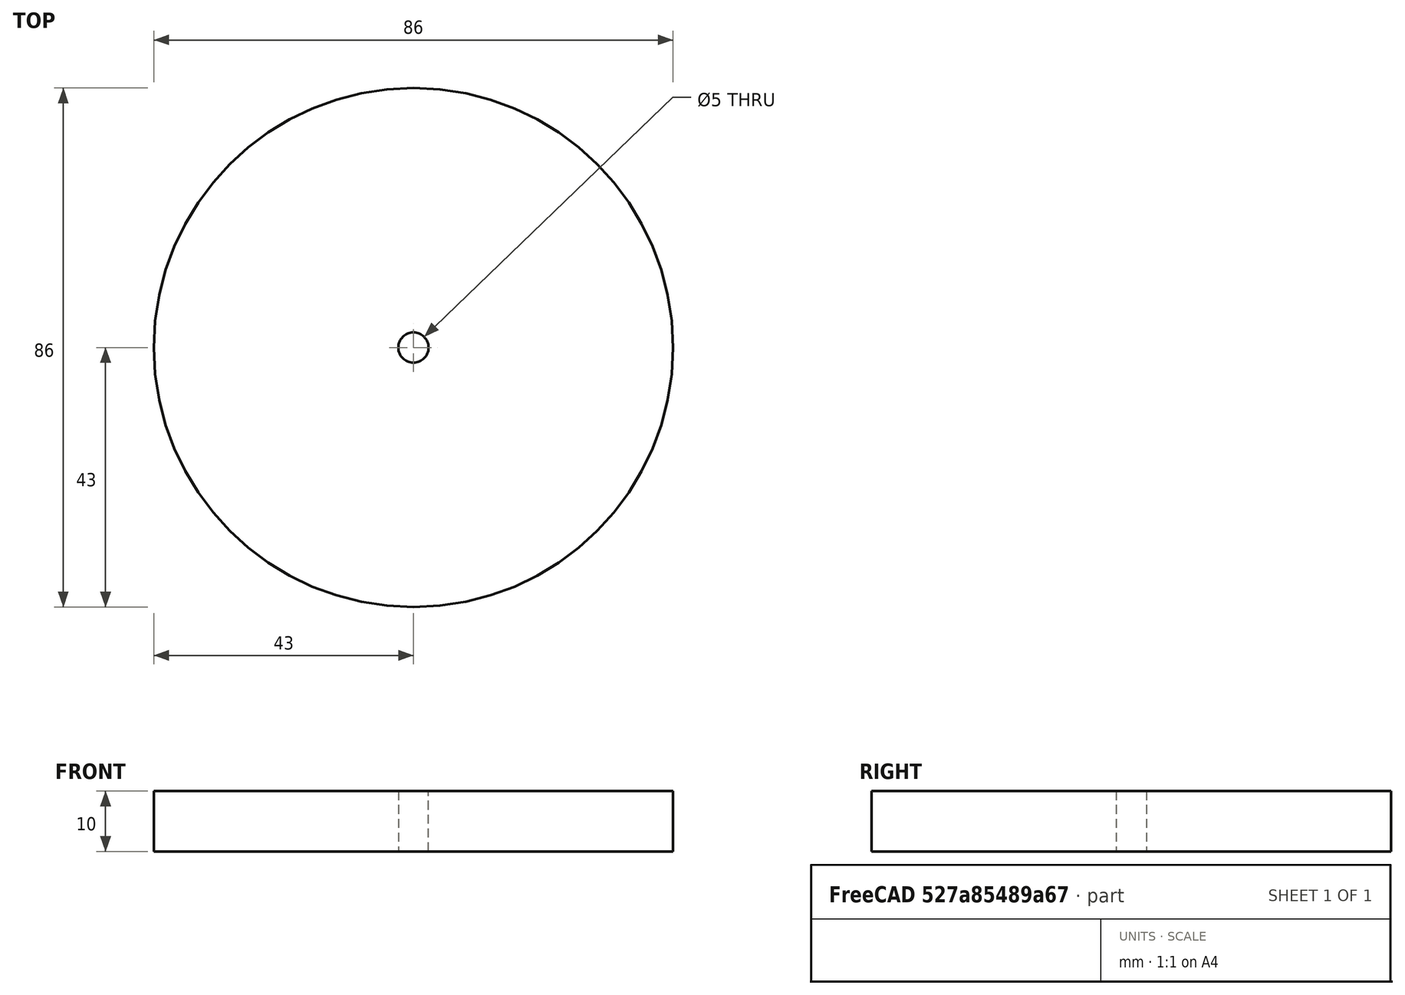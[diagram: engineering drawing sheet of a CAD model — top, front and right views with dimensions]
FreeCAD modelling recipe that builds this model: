
FCSTD DOCUMENT  (FreeCAD 0.19R24276 (Git))
Label: Temp_circle_d86
License: All rights reserved
LicenseURL: http://en.wikipedia.org/wiki/All_rights_reserved
objects: Sketcher::SketchObject×1, PartDesign::Pad×1, PartDesign::Body×1
note: 4 computed .brp shape members not serialized (recipe doc carries the construction recipe); baked Part::Feature solids carry a one-line shape summary decoded from their .brp

FEATURE [Sketcher::SketchObject] Sketch
  FullyConstrained = true
  MapMode = 5
  Support = -> [XY_Plane]
  sketch-geometry (2):
    g0: Circle CenterX=0 CenterY=0 CenterZ=0 NormalX=0 NormalY=0 NormalZ=1 AngleXU=0 Radius=2.5
    g1: Circle CenterX=0 CenterY=0 CenterZ=0 NormalX=0 NormalY=0 NormalZ=1 AngleXU=0 Radius=43
  constraints (4):
    c: Coincident(g0,g-1)
    c: Coincident(g1,g-1)
    c: Diameter(g1) = 86
    c: Diameter(g0) = 5
FEATURE [PartDesign::Pad] Pad
  Direction = (1,1,1)
  Length = 10
  Length2 = 100
  Profile = -> Sketch
  Type = 0
FEATURE [PartDesign::Body] Body
  Group = -> [Sketch,Pad]
  Origin = -> Origin
  Tip = -> Pad
